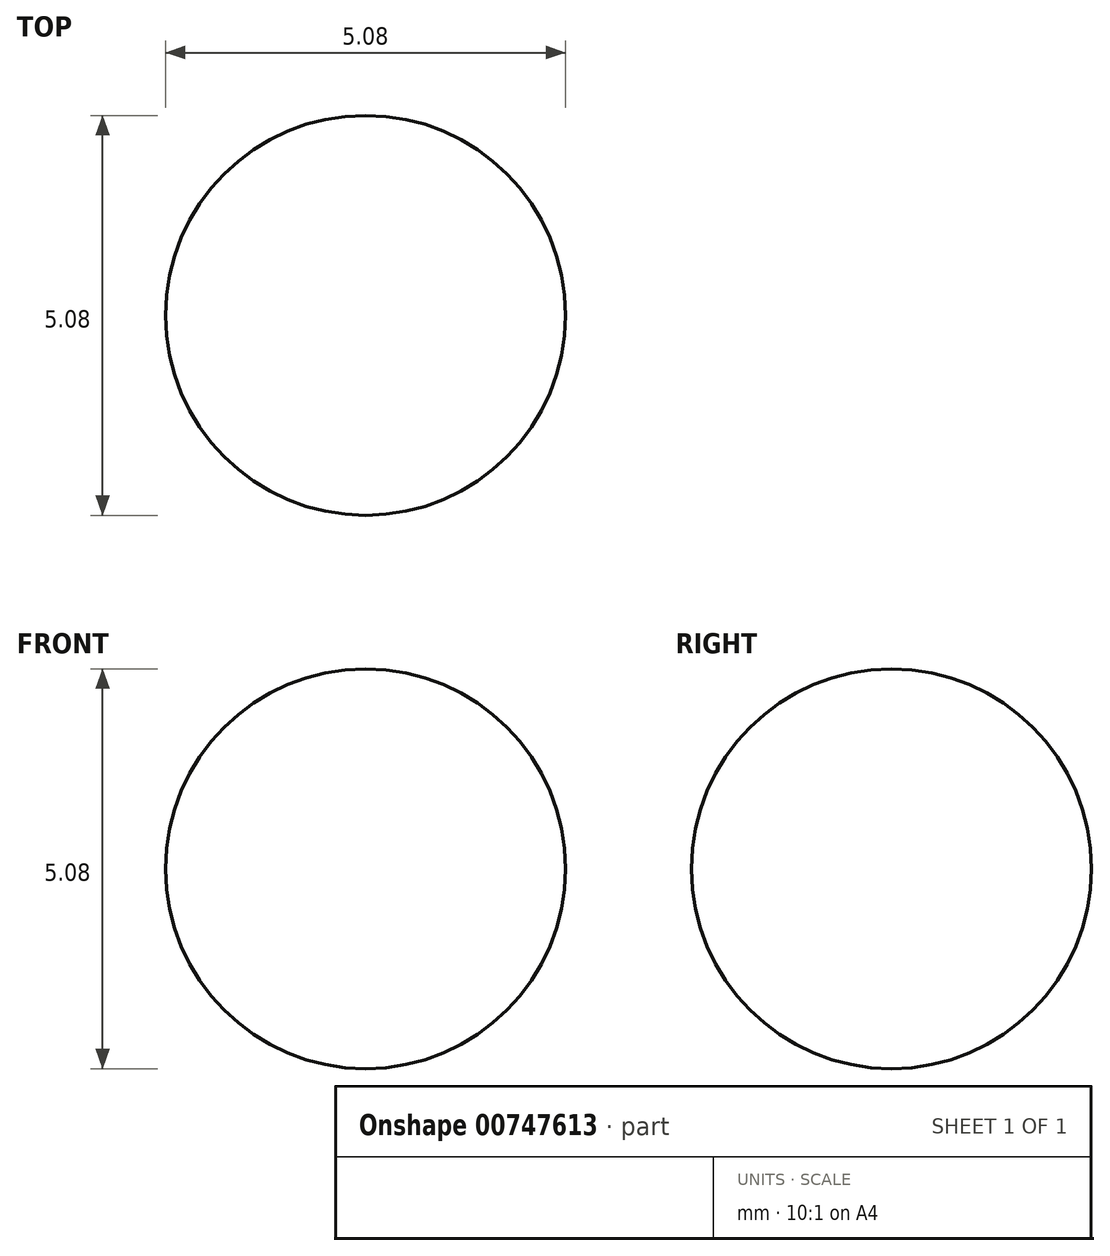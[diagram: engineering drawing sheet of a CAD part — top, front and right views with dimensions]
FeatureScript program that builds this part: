
annotation { "Feature Type Name" : "Feature", "Feature Type Description" : "" }
export const myFeature = defineFeature(function(context is Context, id is Id, definition is map)
    precondition{}
    {
        {
            var Q0;
            Q0=qCreatedBy(makeId("Top.planeOp"),FACE);
            var sketch = newSketch(context, id + "F0", { "sketchPlane" : qUnion([Q0])});
            skArc(sketch, "E0", {"start": v(0, -2.54) * mm, "mid": v(2.54, 0) * mm, "end": v(0, 2.54) * mm});
            skLineSegment(sketch, "E1", {"start": v(0, 2.54) * mm, "end": v(0, -2.54) * mm});
            skSolve(sketch);
        }
        {
            var Q0;
            Q0=makeQuery(id+"F0.imprint","IMPRINT",FACE,{"disambiguationData":[TD([[makeQuery(id+"F0.imprint","IMPRINT",EDGE,{"derivedFrom":sQuery(id+"F0.wireOp",EDGE,"E0")}),1.0]])]});
            var Q1;
            Q1=sQuery(id+"F0.wireOp",EDGE,"E1");
            revolve(context, id + "F1", {"surfaceOperationType" : NewSurfaceOperationType.NEW, "entities" : qUnion([Q0]), "axis" : qUnion([Q1]), "revolveType" : RevolveType.FULL});
        }
    });
